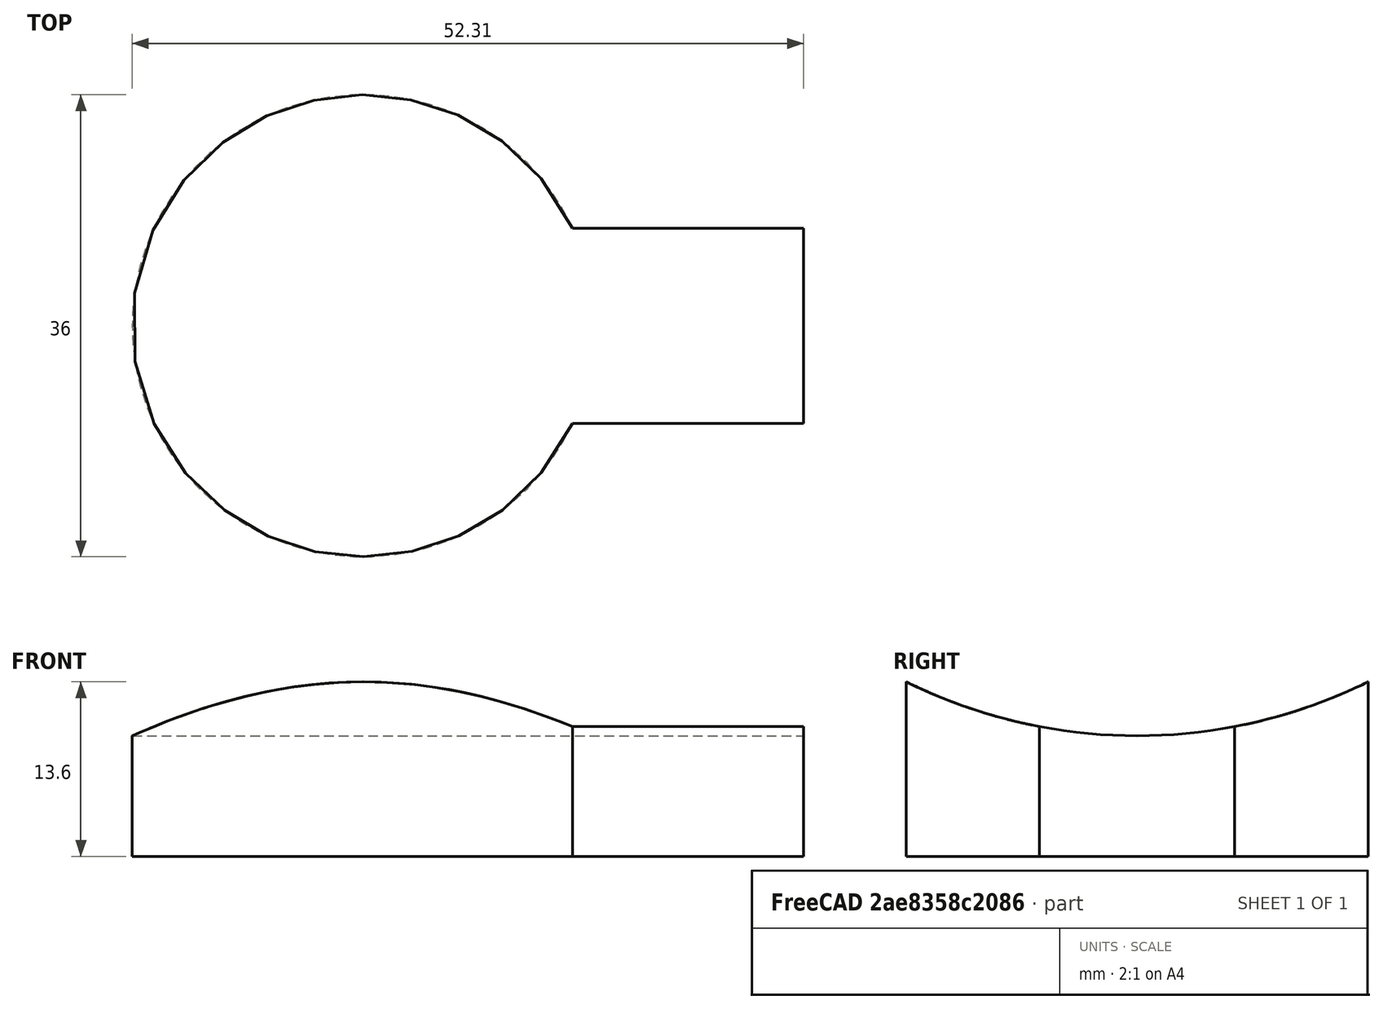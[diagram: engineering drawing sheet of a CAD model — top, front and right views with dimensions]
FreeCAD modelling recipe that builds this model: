
FCSTD DOCUMENT  (FreeCAD 0.19R24291 (Git))
Label: bruker7t_fus_single_coil_wrap_case
License: All rights reserved
LicenseURL: http://en.wikipedia.org/wiki/All_rights_reserved
objects: TechDraw::DrawViewDimension×6, Sketcher::SketchObject×5, TechDraw::DrawViewPart×3, PartDesign::Body×2, PartDesign::Pad×1, TechDraw::DrawSVGTemplate×1, PartDesign::Pocket×1, TechDraw::DrawPage×1
note: 11 computed .brp shape members not serialized (recipe doc carries the construction recipe); baked Part::Feature solids carry a one-line shape summary decoded from their .brp

FEATURE [Sketcher::SketchObject] Sketch001
  FullyConstrained = true
  MapMode = 5
  sketch-geometry (5):
    g0: LineSegment StartX=29.3135 StartY=7.60713 StartZ=0 EndX=11.3135 EndY=7.60713 EndZ=0
    g1: ArcOfCircle CenterX=-5 CenterY=-1.8e-15 CenterZ=0 NormalX=0 NormalY=0 NormalZ=1 AngleXU=0 Radius=18 StartAngle=0.436332 EndAngle=5.84685
    g2: LineSegment StartX=11.3135 StartY=-7.60713 StartZ=0 EndX=29.3135 EndY=-7.60713 EndZ=0
    g3: LineSegment StartX=-5 StartY=-1.8e-15 StartZ=0 EndX=11.3135 EndY=7.60713 EndZ=0
    g4: LineSegment StartX=29.3135 StartY=7.60713 StartZ=0 EndX=29.3135 EndY=-7.60713 EndZ=0
  constraints (15):
    c: Horizontal(g0)
    c: Coincident(g1,g2)
    c: Horizontal(g2)
    c: Equal(g0,g2)
    c: PointOnObject(g1,g-1)
    c: Radius(g1) = 18
    c: Coincident(g0,g1)
    c: Coincident(g3,g1)
    c: Coincident(g3,g0)
    c: Angle(g-1,g3) = 0.436332
    c: DistanceX(g1,g-1) = 5
    c: DistanceX(g2,g2) = 18
    c: Coincident(g4,g0)
    c: Coincident(g4,g2)
    c: Symmetric(g0,g2,g-1)
FEATURE [Sketcher::SketchObject] Sketch004
  FullyConstrained = true
  MapMode = 5
  sketch-geometry (10):
    g0: Circle CenterX=-5 CenterY=-2.84e-14 CenterZ=0 NormalX=0 NormalY=0 NormalZ=1 AngleXU=0 Radius=16
    g1: LineSegment StartX=28.6486 StartY=6.64243 StartZ=0 EndX=10.6486 EndY=6.64243 EndZ=0
    g2: ArcOfCircle CenterX=-5 CenterY=-2.84e-14 CenterZ=0 NormalX=0 NormalY=0 NormalZ=1 AngleXU=0 Radius=17 StartAngle=0.401426 EndAngle=5.88176
    g3: LineSegment StartX=10.6486 StartY=-6.64243 StartZ=0 EndX=28.6486 EndY=-6.64243 EndZ=0
    g4: LineSegment StartX=10.6486 StartY=-6.64243 StartZ=0 EndX=-5 EndY=-2.84e-14 EndZ=0
    g5: LineSegment StartX=28.6486 StartY=6.64243 StartZ=0 EndX=28.6486 EndY=1 EndZ=0
    g6: LineSegment StartX=28.6486 StartY=1 StartZ=0 EndX=32.6486 EndY=1 EndZ=0
    g7: LineSegment StartX=32.6486 StartY=1 StartZ=0 EndX=32.6486 EndY=-1 EndZ=0
    g8: LineSegment StartX=32.6486 StartY=-1 StartZ=0 EndX=28.6486 EndY=-1 EndZ=0
    g9: LineSegment StartX=28.6486 StartY=-1 StartZ=0 EndX=28.6486 EndY=-6.64243 EndZ=0
  constraints (27):
    c: Radius(g0) = 16
    c: DistanceX(g0,g-1) = 5
    c: Horizontal(g1)
    c: Coincident(g2,g3)
    c: Horizontal(g3)
    c: Coincident(g2,g1)
    c: Coincident(g2,g0)
    c: Radius(g2) = 17
    c: Symmetric(g2,g1,g-1)
    c: DistanceX(g1,g1) = 18
    c: Coincident(g4,g2)
    c: Coincident(g4,g2)
    c: Angle(g4,g-1) = 0.401426
    c: Equal(g3,g1)
    c: Coincident(g1,g5)
    c: Vertical(g5)
    c: Coincident(g5,g6)
    c: Horizontal(g6)
    c: Coincident(g6,g7)
    c: Coincident(g7,g8)
    c: Horizontal(g8)
    c: Coincident(g8,g9)
    c: Coincident(g9,g3)
    c: Vertical(g9)
    c: Symmetric(g6,g7,g-1)
    c: DistanceY(g7,g7) = 2
    c: DistanceX(g6,g6) = 4
FEATURE [PartDesign::Pad] Pad
  Direction = (1,1,1)
  Length = 25
  Length2 = 100
  Profile = -> Sketch001
  Refine = true
  Type = 0
FEATURE [Sketcher::SketchObject] Sketch005
  FullyConstrained = true
  MapMode = 5
  Placement = pos=(0,0,1) rot=(0,0,1;0rad)
  sketch-geometry (2):
    g0: Circle CenterX=-5 CenterY=0 CenterZ=0 NormalX=0 NormalY=0 NormalZ=1 AngleXU=0 Radius=16
    g1: Circle CenterX=-5 CenterY=0 CenterZ=0 NormalX=0 NormalY=0 NormalZ=1 AngleXU=0 Radius=15
  constraints (5):
    c: Radius(g0) = 16
    c: PointOnObject(g0,g-1)
    c: DistanceX(g0,g-1) = 5
    c: Coincident(g0,g1)
    c: Radius(g1) = 15
FEATURE [Sketcher::SketchObject] Sketch006
  FullyConstrained = true
  MapMode = 5
  sketch-geometry (2):
    g0: Circle CenterX=-5 CenterY=0 CenterZ=0 NormalX=0 NormalY=0 NormalZ=1 AngleXU=0 Radius=16
    g1: Circle CenterX=-5 CenterY=0 CenterZ=0 NormalX=0 NormalY=0 NormalZ=1 AngleXU=0 Radius=14
  constraints (5):
    c: Radius(g0) = 16
    c: PointOnObject(g0,g-1)
    c: DistanceX(g0,g-1) = 5
    c: Coincident(g0,g1)
    c: Radius(g1) = 14
FEATURE [TechDraw::DrawSVGTemplate] Template
  Height = 297
  Orientation = 1
  Width = 420
FEATURE [PartDesign::Body] Body001
  Origin = -> Origin002
FEATURE [Sketcher::SketchObject] Sketch
  ExternalGeometry = -> [Pad]
  FullyConstrained = false
  MapMode = 5
  Placement = pos=(0,0,0) rot=(0.57735,0.57735,0.57735;2.0944rad)
  Support = -> [YZ_Plane001]
  sketch-geometry (3):
    g0: ArcOfCircle CenterX=8e-16 CenterY=50 CenterZ=0 NormalX=0 NormalY=0 NormalZ=1 AngleXU=0 Radius=40.6081 StartAngle=3.80479 EndAngle=5.61999
    g1: LineSegment StartX=8e-16 StartY=50 StartZ=0 EndX=32.0003 EndY=25 EndZ=0
    g2: LineSegment StartX=-32.0003 StartY=25 StartZ=0 EndX=0 EndY=50 EndZ=0
  constraints (7):
    c: Coincident(g0,g1)
    c: Coincident(g0,g1)
    c: Coincident(g0,g2)
    c: Coincident(g0,g2)
    c: Symmetric(g0,g0,g-2)
    c: DistanceY(g-1,g0) = 25
    c: DistanceY(g-1,g0) = 50
FEATURE [PartDesign::Pocket] Pocket
  BaseFeature = -> Pad
  Length = 5
  Length2 = 100
  Midplane = true
  Profile = -> Sketch
  Refine = true
  Type = 1
FEATURE [PartDesign::Body] Body
  Group = -> [Sketch001,Pad,Pocket,Sketch004,Sketch005,Sketch006,Sketch]
  Origin = -> Origin001
  Tip = -> Pocket
FEATURE [TechDraw::DrawViewPart] View
  CoarseView = false
  Direction = (0,0,1)
  Focus = 100
  HardHidden = false
  IsoCount = 0
  IsoHidden = false
  IsoVisible = false
  LockPosition = false
  Perspective = false
  Rotation = 0
  Scale = 2
  ScaleType = 0
  SeamHidden = false
  SeamVisible = true
  SmoothHidden = false
  SmoothVisible = true
  Source = -> [Body]
  X = 92.1593
  XDirection = (1,0,0)
  Y = 166.895
FEATURE [TechDraw::DrawViewDimension] Dimension
  Arbitrary = false
  ArbitraryTolerances = false
  EqualTolerance = true
  FormatSpec = %.2f
  FormatSpecOverTolerance = %+.2f
  FormatSpecUnderTolerance = %+.2f
  Inverted = false
  LockPosition = false
  MeasureType = 1
  OverTolerance = 0
  References2D = -> [View]
  Rotation = 0
  Scale = 2
  ScaleType = 0
  TheoreticalExact = false
  Type = 2
  UnderTolerance = 0
  X = 43.3787
  Y = -1.0347
FEATURE [TechDraw::DrawViewDimension] Dimension001
  Arbitrary = false
  ArbitraryTolerances = false
  EqualTolerance = true
  FormatSpec = R%.2f
  FormatSpecOverTolerance = %+.2f
  FormatSpecUnderTolerance = %+.2f
  Inverted = false
  LockPosition = false
  MeasureType = 1
  OverTolerance = 0
  References2D = -> [View]
  Rotation = 0
  Scale = 2
  ScaleType = 0
  TheoreticalExact = false
  Type = 4
  UnderTolerance = 0
  X = 0
  Y = 0
FEATURE [TechDraw::DrawViewDimension] Dimension002
  Arbitrary = false
  ArbitraryTolerances = false
  EqualTolerance = true
  FormatSpec = R%.2f
  FormatSpecOverTolerance = %+.2f
  FormatSpecUnderTolerance = %+.2f
  Inverted = false
  LockPosition = false
  MeasureType = 1
  OverTolerance = 0
  References2D = -> [View]
  Rotation = 0
  Scale = 2
  ScaleType = 0
  TheoreticalExact = false
  Type = 4
  UnderTolerance = 0
  X = -28.1668
  Y = 0.6898
FEATURE [TechDraw::DrawViewDimension] Dimension003
  Arbitrary = false
  ArbitraryTolerances = false
  EqualTolerance = true
  FormatSpec = %.2f
  FormatSpecOverTolerance = %+.2f
  FormatSpecUnderTolerance = %+.2f
  Inverted = false
  LockPosition = false
  MeasureType = 1
  OverTolerance = 0
  References2D = -> [View]
  Rotation = 0
  Scale = 2
  ScaleType = 0
  TheoreticalExact = false
  Type = 1
  UnderTolerance = 0
  X = 35.2356
  Y = 26.8606
FEATURE [TechDraw::DrawViewPart] View001
  CoarseView = false
  Direction = (0.079,0.539,-0.838)
  Focus = 100
  HardHidden = false
  IsoCount = 0
  IsoHidden = false
  IsoVisible = false
  LockPosition = false
  Perspective = false
  Rotation = 0
  Scale = 2
  ScaleType = 0
  SeamHidden = false
  SeamVisible = true
  SmoothHidden = false
  SmoothVisible = true
  Source = -> [Body]
  X = 289.04
  XDirection = (0.777,-0.56,-0.287)
  Y = 166.32
FEATURE [TechDraw::DrawViewPart] View002
  CoarseView = false
  Direction = (1,0,0)
  Focus = 100
  HardHidden = false
  IsoCount = 0
  IsoHidden = false
  IsoVisible = false
  LockPosition = false
  Perspective = false
  Rotation = 0
  Scale = 2
  ScaleType = 0
  SeamHidden = false
  SeamVisible = true
  SmoothHidden = false
  SmoothVisible = true
  Source = -> [Body]
  X = 79.513
  XDirection = (0,1,0)
  Y = 84.4061
FEATURE [TechDraw::DrawViewDimension] Dimension004
  Arbitrary = false
  ArbitraryTolerances = false
  EqualTolerance = true
  FormatSpec = %.2f
  FormatSpecOverTolerance = %+.2f
  FormatSpecUnderTolerance = %+.2f
  Inverted = false
  LockPosition = false
  MeasureType = 1
  OverTolerance = 0
  References2D = -> [View002]
  Rotation = 0
  Scale = 2
  ScaleType = 0
  TheoreticalExact = false
  Type = 2
  UnderTolerance = 0
  X = 37.0867
  Y = 18.6821
FEATURE [TechDraw::DrawViewDimension] Dimension005
  Arbitrary = false
  ArbitraryTolerances = false
  EqualTolerance = true
  FormatSpec = %.2f
  FormatSpecOverTolerance = %+.2f
  FormatSpecUnderTolerance = %+.2f
  Inverted = false
  LockPosition = false
  MeasureType = 1
  OverTolerance = 0
  References2D = -> [View002]
  Rotation = 0
  Scale = 2
  ScaleType = 0
  TheoreticalExact = false
  Type = 2
  UnderTolerance = 0
  X = -42.6106
  Y = 1.51191
FEATURE [TechDraw::DrawPage] Page
  KeepUpdated = true
  NextBalloonIndex = 1
  ProjectionType = 0
  Scale = 2
  Template = -> Template
  Views = -> [View,Dimension,Dimension001,Dimension002,Dimension003,View001,View002,Dimension004,Dimension005]
